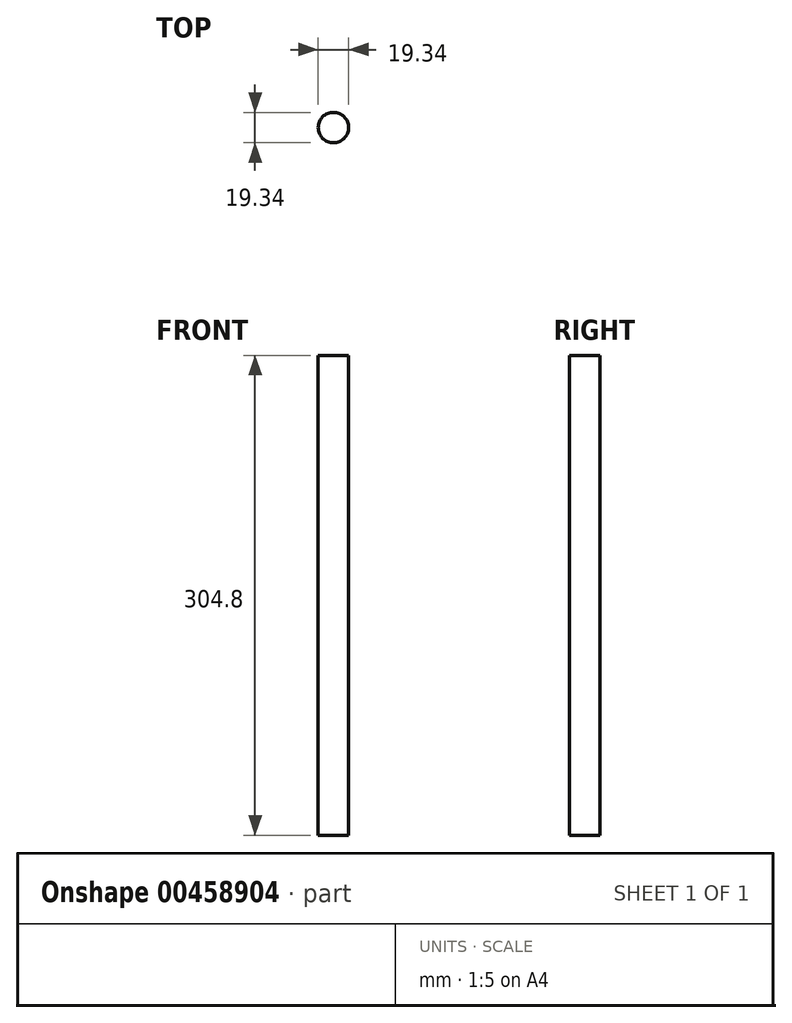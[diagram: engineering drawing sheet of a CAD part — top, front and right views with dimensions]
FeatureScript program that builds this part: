
annotation { "Feature Type Name" : "Feature", "Feature Type Description" : "" }
export const myFeature = defineFeature(function(context is Context, id is Id, definition is map)
    precondition{}
    {
        {
            var Q0;
            Q0=qCreatedBy(makeId("Top.planeOp"),FACE);
            var sketch = newSketch(context, id + "F0", { "sketchPlane" : qUnion([Q0])});
            skCircle(sketch, "E0", {"center": v(0, 0) * mm, "radius": 9.67 * mm});
            skSolve(sketch);
        }
        {
            var Q0;
            Q0=makeQuery(id+"F0.imprint","IMPRINT",FACE,{"disambiguationData":[TD([[makeQuery(id+"F0.imprint","IMPRINT",EDGE,{"derivedFrom":sQuery(id+"F0.wireOp",EDGE,"E0")}),1.0]])]});
            extrude(context, id + "F1", {"entities" : qUnion([Q0]), "depth" : 304.8 * mm});
        }
    });
